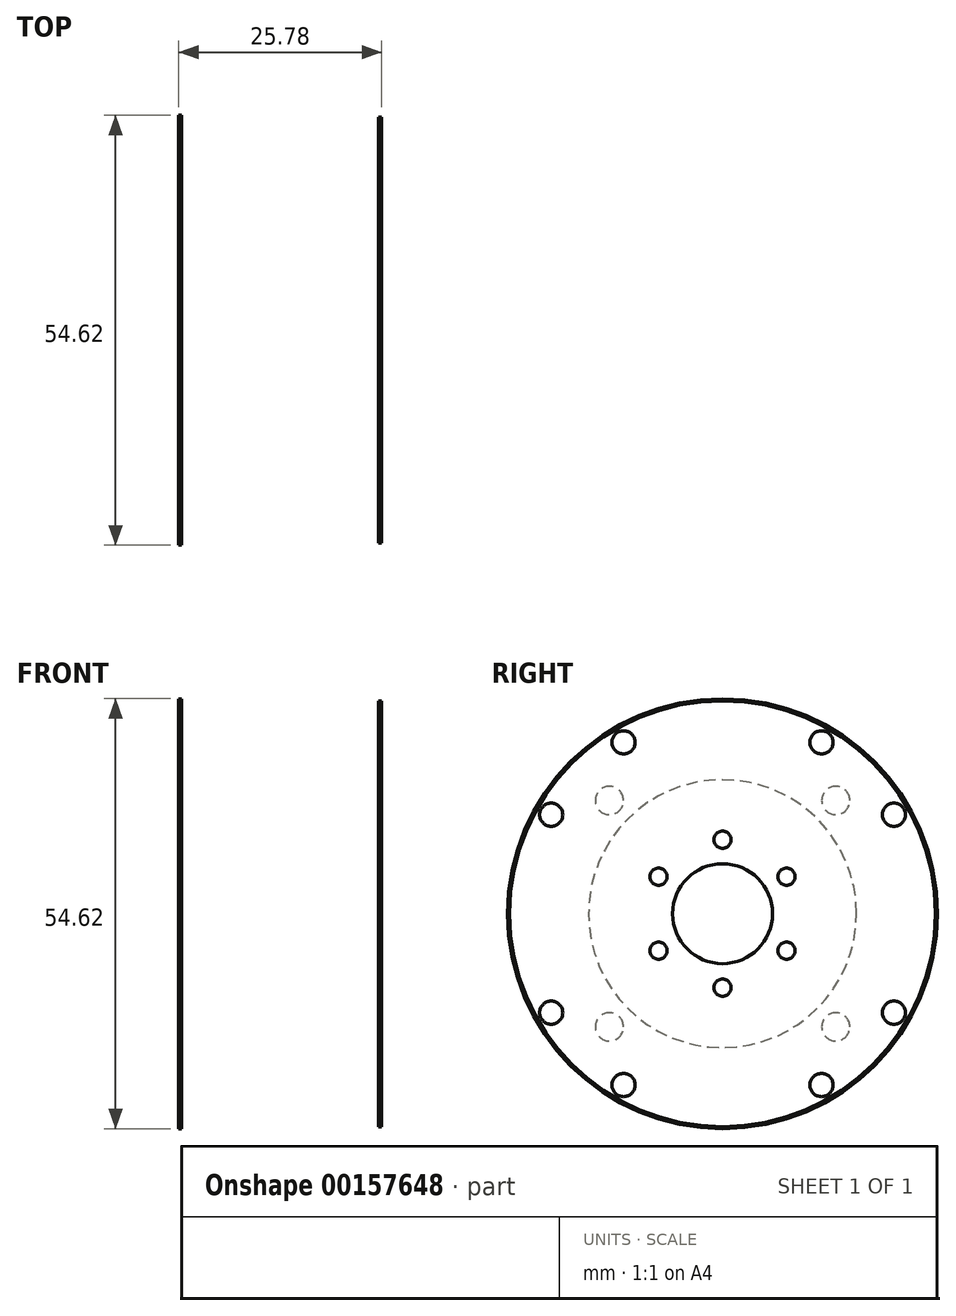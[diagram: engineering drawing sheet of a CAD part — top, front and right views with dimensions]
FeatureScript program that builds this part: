
annotation { "Feature Type Name" : "Feature", "Feature Type Description" : "" }
export const myFeature = defineFeature(function(context is Context, id is Id, definition is map)
    precondition{}
    {
        {
            var Q0;
            Q0=qCreatedBy(makeId("Right.planeOp"),FACE);
            var sketch = newSketch(context, id + "F0", { "sketchPlane" : qUnion([Q0])});
            skCircle(sketch, "E0", {"center": v(0, 0) * mm, "radius": 27.3 * mm});
            skCircle(sketch, "E1", {"center": v(0, 0) * mm, "radius": 17.02 * mm});
            skCircle(sketch, "E2", {"center": v(12.57, 21.77) * mm, "radius": 1.47 * mm});
            skCircle(sketch, "E3", {"center": v(21.77, 12.57) * mm, "radius": 1.47 * mm});
            skCircle(sketch, "E4", {"center": v(14.38, 14.38) * mm, "radius": 1.8 * mm});
            skCircle(sketch, "E5.MirrorC", {"center": v(-12.57, 21.77) * mm, "radius": 1.47 * mm});
            skCircle(sketch, "E6.MirrorC", {"center": v(-14.38, 14.38) * mm, "radius": 1.8 * mm});
            skCircle(sketch, "E7.MirrorC", {"center": v(-21.77, 12.57) * mm, "radius": 1.47 * mm});
            skCircle(sketch, "E8.MirrorC", {"center": v(-21.77, -12.57) * mm, "radius": 1.47 * mm});
            skCircle(sketch, "E9.MirrorC", {"center": v(-14.38, -14.38) * mm, "radius": 1.8 * mm});
            skCircle(sketch, "E10.MirrorC", {"center": v(-12.57, -21.77) * mm, "radius": 1.47 * mm});
            skCircle(sketch, "E11.MirrorC", {"center": v(12.57, -21.77) * mm, "radius": 1.47 * mm});
            skCircle(sketch, "E12.MirrorC", {"center": v(14.38, -14.38) * mm, "radius": 1.8 * mm});
            skCircle(sketch, "E13.MirrorC", {"center": v(21.77, -12.57) * mm, "radius": 1.47 * mm});
            skSolve(sketch);
        }
        {
            var Q0;
            Q0=makeQuery(id+"F0.imprint","IMPRINT",FACE,{"disambiguationData":[TD([[makeQuery(id+"F0.imprint","IMPRINT",EDGE,{"derivedFrom":sQuery(id+"F0.wireOp",EDGE,"E0")}),1.0]])]});
            extrude(context, id + "F1", {"entities" : qUnion([Q0]), "oppositeDirection" : true, "depth" : 0.38 * mm});
        }
        {
            var Q0;
            Q0=qCreatedBy(makeId("Right.planeOp"),FACE);
            cPlane(context, id + "F2", {"entities" : qUnion([Q0]), "cplaneType" : CPlaneType.OFFSET, "offset" : 25.4 * mm, "width" : 152.4 * mm, "height" : 152.4 * mm});
        }
        {
            var Q0;
            Q0=qCreatedBy(id+"F2.planeOp",FACE);
            var sketch = newSketch(context, id + "F3", { "sketchPlane" : qUnion([Q0])});
            skCircle(sketch, "E14", {"center": v(0, 0) * mm, "radius": 27.05 * mm});
            skCircle(sketch, "E15", {"center": v(0, 0) * mm, "radius": 6.35 * mm});
            skCircle(sketch, "E16", {"center": v(12.57, 21.77) * mm, "radius": 1.47 * mm});
            skCircle(sketch, "E17", {"center": v(21.77, 12.57) * mm, "radius": 1.47 * mm});
            skCircle(sketch, "E18", {"center": v(0, 9.4) * mm, "radius": 1.1 * mm});
            skCircle(sketch, "E19", {"center": v(8.13, 4.7) * mm, "radius": 1.1 * mm});
            skCircle(sketch, "E20.MirrorC", {"center": v(-12.57, 21.77) * mm, "radius": 1.47 * mm});
            skCircle(sketch, "E21.MirrorC", {"center": v(-21.77, 12.57) * mm, "radius": 1.47 * mm});
            skCircle(sketch, "E22.MirrorC", {"center": v(-8.13, 4.7) * mm, "radius": 1.1 * mm});
            skCircle(sketch, "E23.MirrorC", {"center": v(-21.77, -12.57) * mm, "radius": 1.47 * mm});
            skCircle(sketch, "E24.MirrorC", {"center": v(-8.13, -4.7) * mm, "radius": 1.1 * mm});
            skCircle(sketch, "E25.MirrorC", {"center": v(-12.57, -21.77) * mm, "radius": 1.47 * mm});
            skCircle(sketch, "E26.MirrorC", {"center": v(0, -9.4) * mm, "radius": 1.1 * mm});
            skCircle(sketch, "E27.MirrorC", {"center": v(8.13, -4.7) * mm, "radius": 1.1 * mm});
            skCircle(sketch, "E28.MirrorC", {"center": v(12.57, -21.77) * mm, "radius": 1.47 * mm});
            skCircle(sketch, "E29.MirrorC", {"center": v(21.77, -12.57) * mm, "radius": 1.47 * mm});
            skSolve(sketch);
        }
        {
            var Q0;
            Q0=makeQuery(id+"F3.imprint","IMPRINT",FACE,{"disambiguationData":[TD([[makeQuery(id+"F3.imprint","IMPRINT",EDGE,{"derivedFrom":sQuery(id+"F3.wireOp",EDGE,"E14")}),1.0]])]});
            extrude(context, id + "F4", {"entities" : qUnion([Q0]), "oppositeDirection" : true, "depth" : 0.38 * mm});
        }
    });
